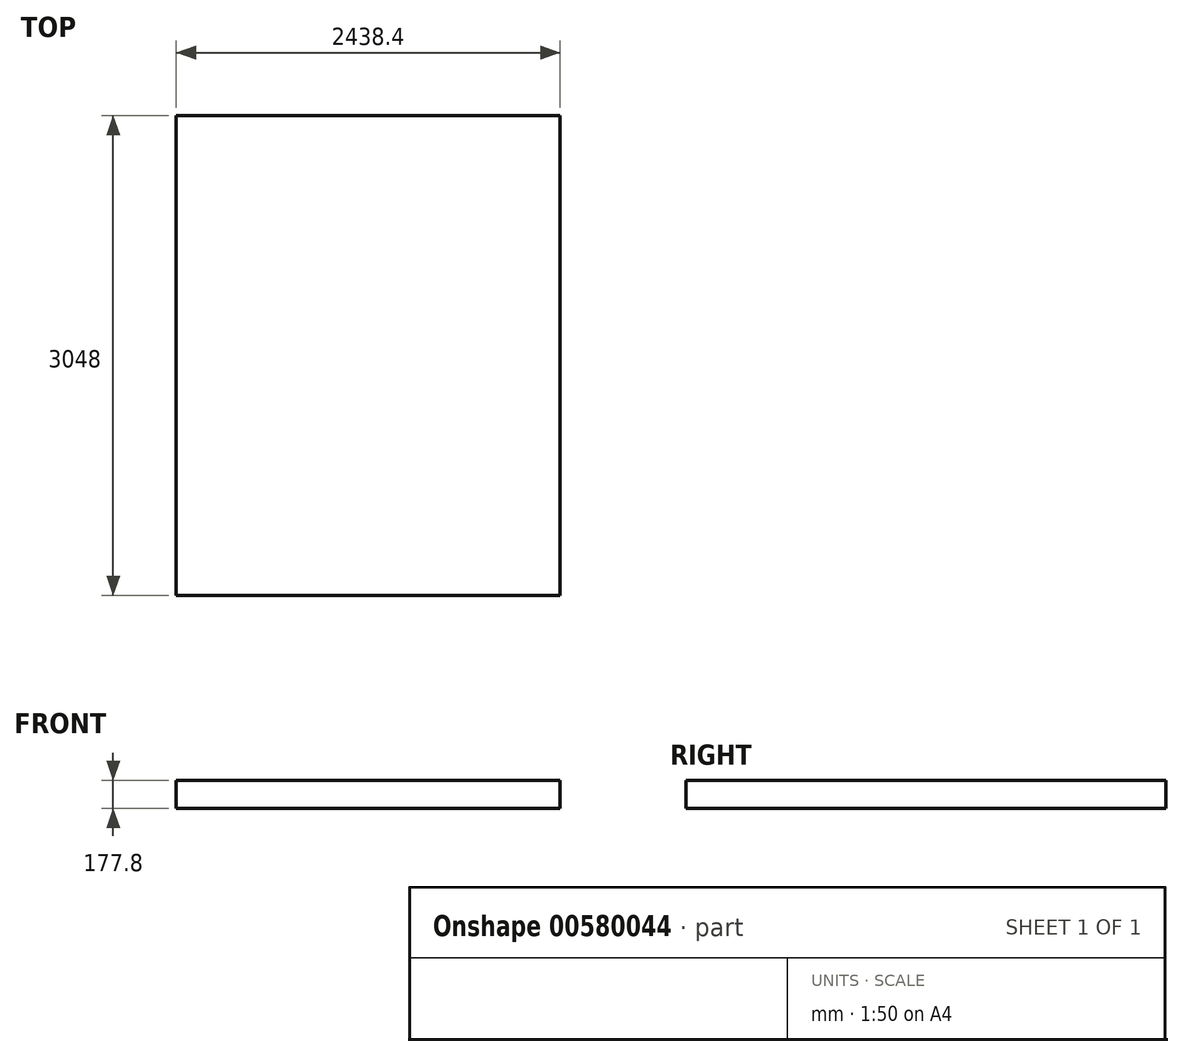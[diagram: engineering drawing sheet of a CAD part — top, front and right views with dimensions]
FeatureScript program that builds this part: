
annotation { "Feature Type Name" : "Feature", "Feature Type Description" : "" }
export const myFeature = defineFeature(function(context is Context, id is Id, definition is map)
    precondition{}
    {
        {
            var Q0;
            Q0=qCreatedBy(makeId("Top.planeOp"),FACE);
            var sketch = newSketch(context, id + "F0", { "sketchPlane" : qUnion([Q0])});
            skLineSegment(sketch, "E0.bottom", {"start": v(-591.94, 2150.34) * mm, "end": v(1846.46, 2150.34) * mm});
            skLineSegment(sketch, "E0.top", {"start": v(-591.94, -897.66) * mm, "end": v(1846.46, -897.66) * mm});
            skLineSegment(sketch, "E0.left", {"start": v(-591.94, 2150.34) * mm, "end": v(-591.94, -897.66) * mm});
            skLineSegment(sketch, "E0.right", {"start": v(1846.46, 2150.34) * mm, "end": v(1846.46, -897.66) * mm});
            skSolve(sketch);
        }
        {
            var Q0;
            Q0 = qSketchRegion(id + "F0", true);
            extrude(context, id + "F1", {"entities" : qUnion([Q0]), "depth" : 177.8 * mm, "offsetDistance" : 30.48 * mm});
        }
    });
